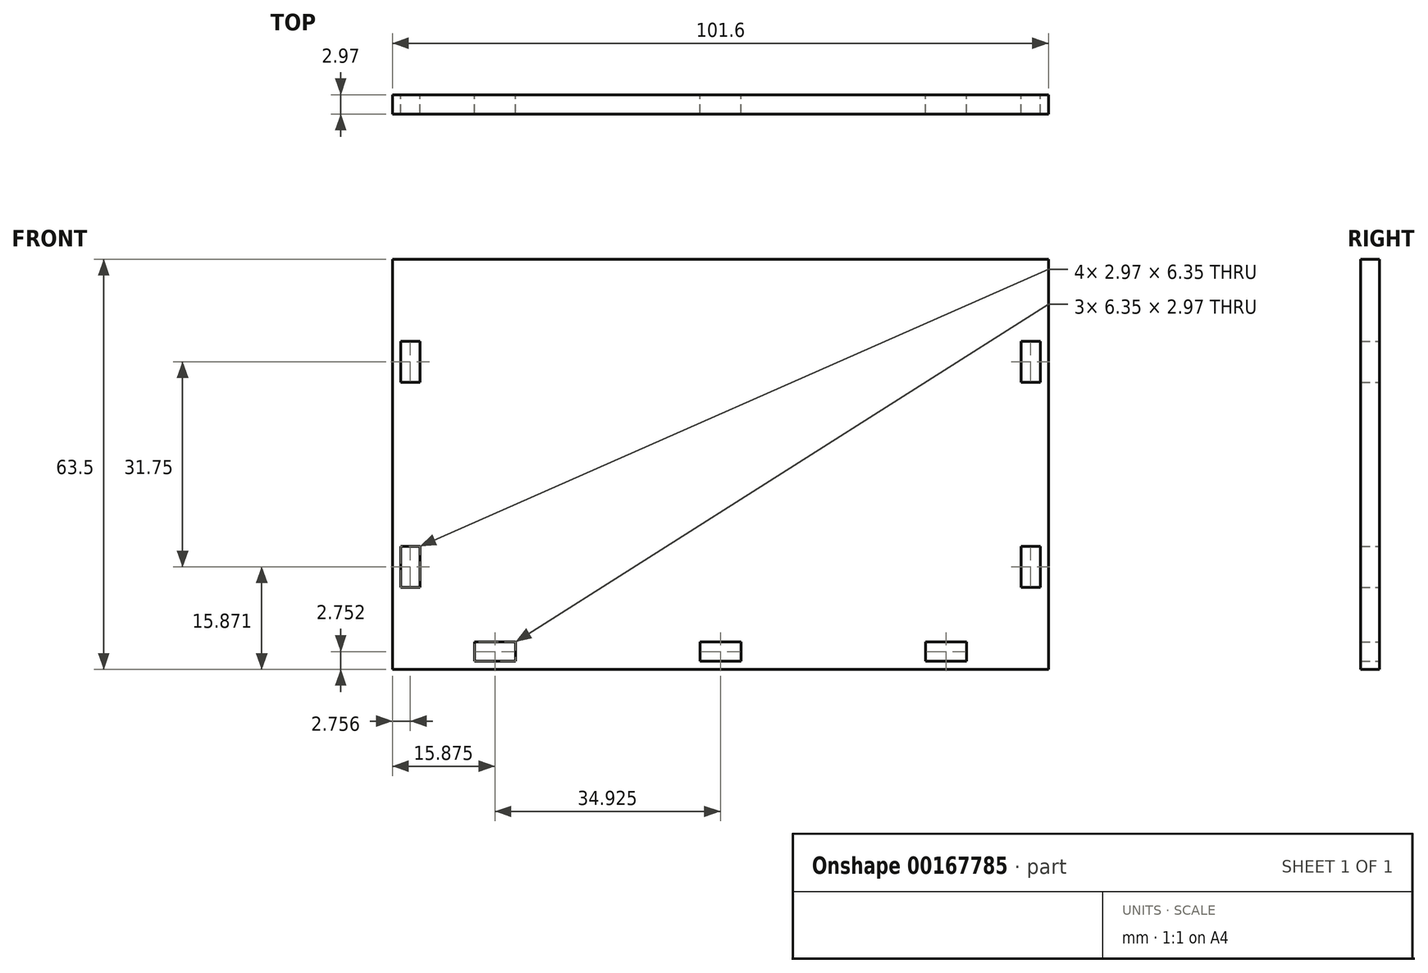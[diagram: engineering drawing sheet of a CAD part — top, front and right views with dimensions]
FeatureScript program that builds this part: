
annotation { "Feature Type Name" : "Feature", "Feature Type Description" : "" }
export const myFeature = defineFeature(function(context is Context, id is Id, definition is map)
    precondition{}
    {
        {
            var Q0;
            Q0=qCreatedBy(makeId("Front.planeOp"),FACE);
            var sketch = newSketch(context, id + "F0", { "sketchPlane" : qUnion([Q0])});
            skLineSegment(sketch, "E0.bottom", {"start": v(50.82, 36.32) * mm, "end": v(-50.78, 36.32) * mm});
            skLineSegment(sketch, "E0.top", {"start": v(50.82, -27.18) * mm, "end": v(-50.78, -27.18) * mm});
            skLineSegment(sketch, "E0.left", {"start": v(50.82, 36.32) * mm, "end": v(50.82, -27.18) * mm});
            skLineSegment(sketch, "E0.right", {"start": v(-50.78, 36.32) * mm, "end": v(-50.78, -27.18) * mm});
            skPoint(sketch, "E0.middle", {"position": v(0.02, 4.57) * mm});
            skLineSegment(sketch, "E1.bottom", {"start": v(-38.08, -22.94) * mm, "end": v(-31.73, -22.94) * mm});
            skLineSegment(sketch, "E1.top", {"start": v(-38.08, -25.91) * mm, "end": v(-31.73, -25.91) * mm});
            skLineSegment(sketch, "E1.left", {"start": v(-38.08, -22.94) * mm, "end": v(-38.08, -25.91) * mm});
            skLineSegment(sketch, "E1.right", {"start": v(-31.73, -22.94) * mm, "end": v(-31.73, -25.91) * mm});
            skLineSegment(sketch, "E2", {"start": v(0.02, 36.32) * mm, "end": v(0.02, -27.18) * mm, "construction": true});
            skLineSegment(sketch, "E3", {"start": v(-50.78, 4.57) * mm, "end": v(50.82, 4.57) * mm, "construction": true});
            skLineSegment(sketch, "E4.MirrorCS", {"start": v(38.12, -22.94) * mm, "end": v(31.77, -22.94) * mm});
            skLineSegment(sketch, "E5.MirrorCS", {"start": v(38.12, -25.91) * mm, "end": v(31.77, -25.91) * mm});
            skLineSegment(sketch, "E6.MirrorCS", {"start": v(31.77, -22.94) * mm, "end": v(31.77, -25.91) * mm});
            skLineSegment(sketch, "E7.MirrorCS", {"start": v(38.12, -22.94) * mm, "end": v(38.12, -25.91) * mm});
            skLineSegment(sketch, "E8.bottom", {"start": v(-3.15, -22.94) * mm, "end": v(3.2, -22.94) * mm});
            skLineSegment(sketch, "E8.top", {"start": v(-3.15, -25.91) * mm, "end": v(3.2, -25.91) * mm});
            skLineSegment(sketch, "E8.left", {"start": v(-3.15, -22.94) * mm, "end": v(-3.15, -25.91) * mm});
            skLineSegment(sketch, "E8.right", {"start": v(3.2, -22.94) * mm, "end": v(3.2, -25.91) * mm});
            skLineSegment(sketch, "E9.bottom", {"start": v(-49.5, 23.62) * mm, "end": v(-46.54, 23.62) * mm});
            skLineSegment(sketch, "E9.top", {"start": v(-49.5, 17.27) * mm, "end": v(-46.54, 17.27) * mm});
            skLineSegment(sketch, "E9.left", {"start": v(-49.5, 23.62) * mm, "end": v(-49.5, 17.27) * mm});
            skLineSegment(sketch, "E9.right", {"start": v(-46.54, 23.62) * mm, "end": v(-46.54, 17.27) * mm});
            skLineSegment(sketch, "E10.MirrorCS", {"start": v(-49.5, -14.48) * mm, "end": v(-49.5, -8.13) * mm});
            skLineSegment(sketch, "E11.MirrorCS", {"start": v(-46.54, -14.48) * mm, "end": v(-46.54, -8.13) * mm});
            skLineSegment(sketch, "E12.MirrorCS", {"start": v(-49.5, -8.13) * mm, "end": v(-46.54, -8.13) * mm});
            skLineSegment(sketch, "E13.MirrorCS", {"start": v(-49.5, -14.48) * mm, "end": v(-46.54, -14.48) * mm});
            skLineSegment(sketch, "E14.MirrorCS", {"start": v(49.55, 23.62) * mm, "end": v(46.58, 23.62) * mm});
            skLineSegment(sketch, "E15.MirrorCS", {"start": v(49.55, 23.62) * mm, "end": v(49.55, 17.27) * mm});
            skLineSegment(sketch, "E16.MirrorCS", {"start": v(46.58, 23.62) * mm, "end": v(46.58, 17.27) * mm});
            skLineSegment(sketch, "E17.MirrorCS", {"start": v(49.55, 17.27) * mm, "end": v(46.58, 17.27) * mm});
            skLineSegment(sketch, "E18.MirrorCS", {"start": v(49.55, -8.13) * mm, "end": v(46.58, -8.13) * mm});
            skLineSegment(sketch, "E19.MirrorCS", {"start": v(49.55, -14.48) * mm, "end": v(49.55, -8.13) * mm});
            skLineSegment(sketch, "E20.MirrorCS", {"start": v(49.55, -14.48) * mm, "end": v(46.58, -14.48) * mm});
            skLineSegment(sketch, "E21.MirrorCS", {"start": v(46.58, -14.48) * mm, "end": v(46.58, -8.13) * mm});
            skLineSegment(sketch, "E22.bottom", {"start": v(-50.78, 36.32) * mm, "end": v(50.82, 36.32) * mm});
            skLineSegment(sketch, "E22.top", {"start": v(-50.78, 155.95) * mm, "end": v(50.82, 155.95) * mm});
            skLineSegment(sketch, "E22.left", {"start": v(-50.78, 36.32) * mm, "end": v(-50.78, 37.08) * mm});
            skLineSegment(sketch, "E22.right", {"start": v(50.82, 36.32) * mm, "end": v(50.82, 37.08) * mm});
            skLineSegment(sketch, "E23", {"start": v(0.02, 36.32) * mm, "end": v(0.02, 155.95) * mm, "construction": true});
            skLineSegment(sketch, "E24.bottom", {"start": v(-3.15, 155.95) * mm, "end": v(3.2, 155.95) * mm});
            skLineSegment(sketch, "E24.top", {"start": v(-3.15, 158.92) * mm, "end": v(3.2, 158.92) * mm});
            skLineSegment(sketch, "E24.left", {"start": v(-3.15, 155.95) * mm, "end": v(-3.15, 158.92) * mm});
            skLineSegment(sketch, "E24.right", {"start": v(3.2, 155.95) * mm, "end": v(3.2, 158.92) * mm});
            skLineSegment(sketch, "E25", {"start": v(-50.78, 153.92) * mm, "end": v(-25.38, 153.92) * mm});
            skLineSegment(sketch, "E26", {"start": v(-50.78, 151.38) * mm, "end": v(-25.38, 151.38) * mm});
            skArc(sketch, "E27", {"start": v(-25.38, 153.92) * mm, "mid": v(-24.1, 152.65) * mm, "end": v(-25.38, 151.38) * mm});
            skLineSegment(sketch, "E28", {"start": v(50.82, 153.68) * mm, "end": v(25.42, 153.92) * mm});
            skLineSegment(sketch, "E29", {"start": v(50.82, 151.38) * mm, "end": v(25.42, 151.38) * mm});
            skLineSegment(sketch, "E30", {"start": v(-21.57, 153.92) * mm, "end": v(21.61, 153.92) * mm});
            skLineSegment(sketch, "E31", {"start": v(-21.57, 151.38) * mm, "end": v(21.61, 151.38) * mm});
            skArc(sketch, "E32", {"start": v(25.42, 153.92) * mm, "mid": v(24.14, 152.65) * mm, "end": v(25.42, 151.38) * mm});
            skPoint(sketch, "E33", {"position": v(0.02, 153.92) * mm});
            skPoint(sketch, "E34", {"position": v(0.02, 151.38) * mm});
            skArc(sketch, "E35", {"start": v(-21.57, 153.92) * mm, "mid": v(-22.84, 152.65) * mm, "end": v(-21.57, 151.38) * mm});
            skArc(sketch, "E36", {"start": v(21.61, 153.92) * mm, "mid": v(22.88, 152.65) * mm, "end": v(21.61, 151.38) * mm});
            skLineSegment(sketch, "E37", {"start": v(-23.47, 155.95) * mm, "end": v(-23.47, 142.74) * mm, "construction": true});
            skLineSegment(sketch, "E38", {"start": v(-45.06, 149.35) * mm, "end": v(-1.88, 149.35) * mm});
            skPoint(sketch, "E38.startSnap0", {"position": v(-23.47, 149.35) * mm});
            skLineSegment(sketch, "E39.0", {"start": v(-45.06, 146.8) * mm, "end": v(-1.88, 146.8) * mm});
            skArc(sketch, "E40", {"start": v(-45.06, 149.35) * mm, "mid": v(-46.33, 148.08) * mm, "end": v(-45.06, 146.8) * mm});
            skArc(sketch, "E41", {"start": v(-1.88, 149.35) * mm, "mid": v(-0.61, 148.08) * mm, "end": v(-1.88, 146.8) * mm});
            skLineSegment(sketch, "E42", {"start": v(-48.5, 149.35) * mm, "end": v(-50.78, 149.35) * mm});
            skLineSegment(sketch, "E43", {"start": v(-48.5, 146.8) * mm, "end": v(-50.78, 146.8) * mm});
            skArc(sketch, "E44", {"start": v(-48.5, 149.35) * mm, "mid": v(-47.22, 148.08) * mm, "end": v(-48.5, 146.8) * mm});
            skArc(sketch, "E45.MirrorCS", {"start": v(1.93, 149.35) * mm, "mid": v(0.66, 148.08) * mm, "end": v(1.93, 146.8) * mm});
            skLineSegment(sketch, "E46.MirrorCS", {"start": v(45.1, 149.35) * mm, "end": v(1.93, 149.35) * mm});
            skLineSegment(sketch, "E47.MirrorCS", {"start": v(45.1, 146.8) * mm, "end": v(1.93, 146.8) * mm});
            skArc(sketch, "E48.MirrorCS", {"start": v(45.1, 149.35) * mm, "mid": v(46.38, 148.08) * mm, "end": v(45.1, 146.8) * mm});
            skLineSegment(sketch, "E49.MirrorCS", {"start": v(48.53, 149.35) * mm, "end": v(50.82, 149.35) * mm});
            skLineSegment(sketch, "E50.MirrorCS", {"start": v(48.53, 146.8) * mm, "end": v(50.82, 146.8) * mm});
            skArc(sketch, "E51", {"start": v(48.53, 149.35) * mm, "mid": v(47.26, 148.08) * mm, "end": v(48.53, 146.8) * mm});
            skLineSegment(sketch, "E52.1.0.0", {"start": v(50.82, 144.54) * mm, "end": v(25.42, 144.77) * mm});
            skLineSegment(sketch, "E52.1.0.1", {"start": v(-21.57, 144.77) * mm, "end": v(21.61, 144.77) * mm});
            skArc(sketch, "E52.1.0.2", {"start": v(25.42, 144.77) * mm, "mid": v(24.14, 143.5) * mm, "end": v(25.42, 142.23) * mm});
            skArc(sketch, "E52.1.0.3", {"start": v(21.61, 144.77) * mm, "mid": v(22.88, 143.5) * mm, "end": v(21.61, 142.23) * mm});
            skLineSegment(sketch, "E52.1.0.4", {"start": v(50.82, 142.23) * mm, "end": v(25.42, 142.23) * mm});
            skLineSegment(sketch, "E52.1.0.5", {"start": v(48.53, 140.2) * mm, "end": v(50.82, 140.2) * mm});
            skArc(sketch, "E52.1.0.6", {"start": v(48.53, 140.2) * mm, "mid": v(47.26, 138.93) * mm, "end": v(48.53, 137.66) * mm});
            skArc(sketch, "E52.1.0.7", {"start": v(45.1, 140.2) * mm, "mid": v(46.38, 138.93) * mm, "end": v(45.1, 137.66) * mm});
            skLineSegment(sketch, "E52.1.0.8", {"start": v(48.53, 137.66) * mm, "end": v(50.82, 137.66) * mm});
            skLineSegment(sketch, "E52.1.0.9", {"start": v(45.1, 137.66) * mm, "end": v(1.93, 137.66) * mm});
            skLineSegment(sketch, "E52.1.0.10", {"start": v(45.1, 140.2) * mm, "end": v(1.93, 140.2) * mm});
            skLineSegment(sketch, "E52.1.0.11", {"start": v(-21.57, 142.23) * mm, "end": v(21.61, 142.23) * mm});
            skArc(sketch, "E52.1.0.12", {"start": v(1.93, 140.2) * mm, "mid": v(0.66, 138.93) * mm, "end": v(1.93, 137.66) * mm});
            skArc(sketch, "E52.1.0.13", {"start": v(-1.88, 140.2) * mm, "mid": v(-0.61, 138.93) * mm, "end": v(-1.88, 137.66) * mm});
            skLineSegment(sketch, "E52.1.0.14", {"start": v(-45.06, 140.2) * mm, "end": v(-1.88, 140.2) * mm});
            skLineSegment(sketch, "E52.1.0.15", {"start": v(-45.06, 137.66) * mm, "end": v(-1.88, 137.66) * mm});
            skLineSegment(sketch, "E52.1.0.16", {"start": v(-50.78, 144.77) * mm, "end": v(-25.38, 144.77) * mm});
            skArc(sketch, "E52.1.0.17", {"start": v(-25.38, 144.77) * mm, "mid": v(-24.1, 143.5) * mm, "end": v(-25.38, 142.23) * mm});
            skArc(sketch, "E52.1.0.18", {"start": v(-21.57, 144.77) * mm, "mid": v(-22.84, 143.5) * mm, "end": v(-21.57, 142.23) * mm});
            skLineSegment(sketch, "E52.1.0.19", {"start": v(-50.78, 142.23) * mm, "end": v(-25.38, 142.23) * mm});
            skArc(sketch, "E52.1.0.20", {"start": v(-45.06, 140.2) * mm, "mid": v(-46.33, 138.93) * mm, "end": v(-45.06, 137.66) * mm});
            skArc(sketch, "E52.1.0.21", {"start": v(-48.5, 140.2) * mm, "mid": v(-47.22, 138.93) * mm, "end": v(-48.5, 137.66) * mm});
            skLineSegment(sketch, "E52.1.0.22", {"start": v(-48.5, 137.66) * mm, "end": v(-50.78, 137.66) * mm});
            skLineSegment(sketch, "E52.1.0.23", {"start": v(-48.5, 140.2) * mm, "end": v(-50.78, 140.2) * mm});
            skLineSegment(sketch, "E52.2.0.0", {"start": v(50.82, 135.4) * mm, "end": v(25.42, 135.63) * mm});
            skLineSegment(sketch, "E52.2.0.1", {"start": v(-21.57, 135.63) * mm, "end": v(21.61, 135.63) * mm});
            skArc(sketch, "E52.2.0.2", {"start": v(25.42, 135.63) * mm, "mid": v(24.14, 134.36) * mm, "end": v(25.42, 133.1) * mm});
            skArc(sketch, "E52.2.0.3", {"start": v(21.61, 135.63) * mm, "mid": v(22.88, 134.36) * mm, "end": v(21.61, 133.09) * mm});
            skLineSegment(sketch, "E52.2.0.4", {"start": v(50.82, 133.09) * mm, "end": v(25.42, 133.1) * mm});
            skLineSegment(sketch, "E52.2.0.5", {"start": v(48.53, 131.06) * mm, "end": v(50.82, 131.06) * mm});
            skArc(sketch, "E52.2.0.6", {"start": v(48.53, 131.06) * mm, "mid": v(47.26, 129.79) * mm, "end": v(48.53, 128.52) * mm});
            skArc(sketch, "E52.2.0.7", {"start": v(45.1, 131.06) * mm, "mid": v(46.38, 129.79) * mm, "end": v(45.1, 128.52) * mm});
            skLineSegment(sketch, "E52.2.0.8", {"start": v(48.53, 128.52) * mm, "end": v(50.82, 128.52) * mm});
            skLineSegment(sketch, "E52.2.0.9", {"start": v(45.1, 128.52) * mm, "end": v(1.93, 128.52) * mm});
            skLineSegment(sketch, "E52.2.0.10", {"start": v(45.1, 131.06) * mm, "end": v(1.93, 131.06) * mm});
            skLineSegment(sketch, "E52.2.0.11", {"start": v(-21.57, 133.09) * mm, "end": v(21.61, 133.09) * mm});
            skArc(sketch, "E52.2.0.12", {"start": v(1.93, 131.06) * mm, "mid": v(0.66, 129.79) * mm, "end": v(1.93, 128.52) * mm});
            skArc(sketch, "E52.2.0.13", {"start": v(-1.88, 131.06) * mm, "mid": v(-0.61, 129.79) * mm, "end": v(-1.88, 128.52) * mm});
            skLineSegment(sketch, "E52.2.0.14", {"start": v(-45.06, 131.06) * mm, "end": v(-1.88, 131.06) * mm});
            skLineSegment(sketch, "E52.2.0.15", {"start": v(-45.06, 128.52) * mm, "end": v(-1.88, 128.52) * mm});
            skLineSegment(sketch, "E52.2.0.16", {"start": v(-50.78, 135.63) * mm, "end": v(-25.38, 135.63) * mm});
            skArc(sketch, "E52.2.0.17", {"start": v(-25.38, 135.63) * mm, "mid": v(-24.1, 134.36) * mm, "end": v(-25.38, 133.09) * mm});
            skArc(sketch, "E52.2.0.18", {"start": v(-21.57, 135.63) * mm, "mid": v(-22.84, 134.36) * mm, "end": v(-21.57, 133.09) * mm});
            skLineSegment(sketch, "E52.2.0.19", {"start": v(-50.78, 133.09) * mm, "end": v(-25.38, 133.09) * mm});
            skArc(sketch, "E52.2.0.20", {"start": v(-45.06, 131.06) * mm, "mid": v(-46.33, 129.79) * mm, "end": v(-45.06, 128.52) * mm});
            skArc(sketch, "E52.2.0.21", {"start": v(-48.5, 131.06) * mm, "mid": v(-47.22, 129.79) * mm, "end": v(-48.5, 128.52) * mm});
            skLineSegment(sketch, "E52.2.0.22", {"start": v(-48.5, 128.52) * mm, "end": v(-50.78, 128.52) * mm});
            skLineSegment(sketch, "E52.2.0.23", {"start": v(-48.5, 131.06) * mm, "end": v(-50.78, 131.06) * mm});
            skLineSegment(sketch, "E52.3.0.0", {"start": v(50.82, 126.25) * mm, "end": v(25.42, 126.49) * mm});
            skLineSegment(sketch, "E52.3.0.1", {"start": v(-21.57, 126.49) * mm, "end": v(21.61, 126.49) * mm});
            skArc(sketch, "E52.3.0.2", {"start": v(25.42, 126.49) * mm, "mid": v(24.14, 125.22) * mm, "end": v(25.42, 123.95) * mm});
            skArc(sketch, "E52.3.0.3", {"start": v(21.61, 126.49) * mm, "mid": v(22.88, 125.22) * mm, "end": v(21.61, 123.95) * mm});
            skLineSegment(sketch, "E52.3.0.4", {"start": v(50.82, 123.95) * mm, "end": v(25.42, 123.95) * mm});
            skLineSegment(sketch, "E52.3.0.5", {"start": v(48.53, 121.91) * mm, "end": v(50.82, 121.91) * mm});
            skArc(sketch, "E52.3.0.6", {"start": v(48.53, 121.91) * mm, "mid": v(47.26, 120.64) * mm, "end": v(48.53, 119.37) * mm});
            skArc(sketch, "E52.3.0.7", {"start": v(45.1, 121.91) * mm, "mid": v(46.38, 120.64) * mm, "end": v(45.1, 119.37) * mm});
            skLineSegment(sketch, "E52.3.0.8", {"start": v(48.53, 119.37) * mm, "end": v(50.82, 119.37) * mm});
            skLineSegment(sketch, "E52.3.0.9", {"start": v(45.1, 119.37) * mm, "end": v(1.93, 119.37) * mm});
            skLineSegment(sketch, "E52.3.0.10", {"start": v(45.1, 121.91) * mm, "end": v(1.93, 121.91) * mm});
            skLineSegment(sketch, "E52.3.0.11", {"start": v(-21.57, 123.95) * mm, "end": v(21.61, 123.95) * mm});
            skArc(sketch, "E52.3.0.12", {"start": v(1.93, 121.91) * mm, "mid": v(0.66, 120.64) * mm, "end": v(1.93, 119.37) * mm});
            skArc(sketch, "E52.3.0.13", {"start": v(-1.88, 121.91) * mm, "mid": v(-0.61, 120.64) * mm, "end": v(-1.88, 119.37) * mm});
            skLineSegment(sketch, "E52.3.0.14", {"start": v(-45.06, 121.91) * mm, "end": v(-1.88, 121.91) * mm});
            skLineSegment(sketch, "E52.3.0.15", {"start": v(-45.06, 119.37) * mm, "end": v(-1.88, 119.37) * mm});
            skLineSegment(sketch, "E52.3.0.16", {"start": v(-50.78, 126.49) * mm, "end": v(-25.38, 126.49) * mm});
            skArc(sketch, "E52.3.0.17", {"start": v(-25.38, 126.49) * mm, "mid": v(-24.1, 125.22) * mm, "end": v(-25.38, 123.95) * mm});
            skArc(sketch, "E52.3.0.18", {"start": v(-21.57, 126.49) * mm, "mid": v(-22.84, 125.22) * mm, "end": v(-21.57, 123.95) * mm});
            skLineSegment(sketch, "E52.3.0.19", {"start": v(-50.78, 123.95) * mm, "end": v(-25.38, 123.95) * mm});
            skArc(sketch, "E52.3.0.20", {"start": v(-45.06, 121.91) * mm, "mid": v(-46.33, 120.64) * mm, "end": v(-45.06, 119.37) * mm});
            skArc(sketch, "E52.3.0.21", {"start": v(-48.5, 121.91) * mm, "mid": v(-47.22, 120.64) * mm, "end": v(-48.5, 119.37) * mm});
            skLineSegment(sketch, "E52.3.0.22", {"start": v(-48.5, 119.37) * mm, "end": v(-50.78, 119.37) * mm});
            skLineSegment(sketch, "E52.3.0.23", {"start": v(-48.5, 121.91) * mm, "end": v(-50.78, 121.91) * mm});
            skLineSegment(sketch, "E52.4.0.0", {"start": v(50.82, 117.1) * mm, "end": v(25.42, 117.34) * mm});
            skLineSegment(sketch, "E52.4.0.1", {"start": v(-21.57, 117.34) * mm, "end": v(21.61, 117.34) * mm});
            skArc(sketch, "E52.4.0.2", {"start": v(25.42, 117.34) * mm, "mid": v(24.14, 116.07) * mm, "end": v(25.42, 114.8) * mm});
            skArc(sketch, "E52.4.0.3", {"start": v(21.61, 117.34) * mm, "mid": v(22.88, 116.07) * mm, "end": v(21.61, 114.8) * mm});
            skLineSegment(sketch, "E52.4.0.4", {"start": v(50.82, 114.8) * mm, "end": v(25.42, 114.8) * mm});
            skLineSegment(sketch, "E52.4.0.5", {"start": v(48.53, 112.77) * mm, "end": v(50.82, 112.77) * mm});
            skArc(sketch, "E52.4.0.6", {"start": v(48.53, 112.77) * mm, "mid": v(47.26, 111.5) * mm, "end": v(48.53, 110.23) * mm});
            skArc(sketch, "E52.4.0.7", {"start": v(45.1, 112.77) * mm, "mid": v(46.38, 111.5) * mm, "end": v(45.1, 110.23) * mm});
            skLineSegment(sketch, "E52.4.0.8", {"start": v(48.53, 110.23) * mm, "end": v(50.82, 110.23) * mm});
            skLineSegment(sketch, "E52.4.0.9", {"start": v(45.1, 110.23) * mm, "end": v(1.93, 110.23) * mm});
            skLineSegment(sketch, "E52.4.0.10", {"start": v(45.1, 112.77) * mm, "end": v(1.93, 112.77) * mm});
            skLineSegment(sketch, "E52.4.0.11", {"start": v(-21.57, 114.8) * mm, "end": v(21.61, 114.8) * mm});
            skArc(sketch, "E52.4.0.12", {"start": v(1.93, 112.77) * mm, "mid": v(0.66, 111.5) * mm, "end": v(1.93, 110.23) * mm});
            skArc(sketch, "E52.4.0.13", {"start": v(-1.88, 112.77) * mm, "mid": v(-0.61, 111.5) * mm, "end": v(-1.88, 110.23) * mm});
            skLineSegment(sketch, "E52.4.0.14", {"start": v(-45.06, 112.77) * mm, "end": v(-1.88, 112.77) * mm});
            skLineSegment(sketch, "E52.4.0.15", {"start": v(-45.06, 110.23) * mm, "end": v(-1.88, 110.23) * mm});
            skLineSegment(sketch, "E52.4.0.16", {"start": v(-50.78, 117.34) * mm, "end": v(-25.38, 117.34) * mm});
            skArc(sketch, "E52.4.0.17", {"start": v(-25.38, 117.34) * mm, "mid": v(-24.1, 116.07) * mm, "end": v(-25.38, 114.8) * mm});
            skArc(sketch, "E52.4.0.18", {"start": v(-21.57, 117.34) * mm, "mid": v(-22.84, 116.07) * mm, "end": v(-21.57, 114.8) * mm});
            skLineSegment(sketch, "E52.4.0.19", {"start": v(-50.78, 114.8) * mm, "end": v(-25.38, 114.8) * mm});
            skArc(sketch, "E52.4.0.20", {"start": v(-45.06, 112.77) * mm, "mid": v(-46.33, 111.5) * mm, "end": v(-45.06, 110.23) * mm});
            skArc(sketch, "E52.4.0.21", {"start": v(-48.5, 112.77) * mm, "mid": v(-47.22, 111.5) * mm, "end": v(-48.5, 110.23) * mm});
            skLineSegment(sketch, "E52.4.0.22", {"start": v(-48.5, 110.23) * mm, "end": v(-50.78, 110.23) * mm});
            skLineSegment(sketch, "E52.4.0.23", {"start": v(-48.5, 112.77) * mm, "end": v(-50.78, 112.77) * mm});
            skLineSegment(sketch, "E52.5.0.0", {"start": v(50.82, 107.96) * mm, "end": v(25.42, 108.2) * mm});
            skLineSegment(sketch, "E52.5.0.1", {"start": v(-21.57, 108.2) * mm, "end": v(21.61, 108.2) * mm});
            skArc(sketch, "E52.5.0.2", {"start": v(25.42, 108.2) * mm, "mid": v(24.14, 106.93) * mm, "end": v(25.42, 105.66) * mm});
            skArc(sketch, "E52.5.0.3", {"start": v(21.61, 108.2) * mm, "mid": v(22.88, 106.93) * mm, "end": v(21.61, 105.66) * mm});
            skLineSegment(sketch, "E52.5.0.4", {"start": v(50.82, 105.66) * mm, "end": v(25.42, 105.66) * mm});
            skLineSegment(sketch, "E52.5.0.5", {"start": v(48.53, 103.63) * mm, "end": v(50.82, 103.63) * mm});
            skArc(sketch, "E52.5.0.6", {"start": v(48.53, 103.63) * mm, "mid": v(47.26, 102.36) * mm, "end": v(48.53, 101.09) * mm});
            skArc(sketch, "E52.5.0.7", {"start": v(45.1, 103.63) * mm, "mid": v(46.38, 102.36) * mm, "end": v(45.1, 101.09) * mm});
            skLineSegment(sketch, "E52.5.0.8", {"start": v(48.53, 101.09) * mm, "end": v(50.82, 101.09) * mm});
            skLineSegment(sketch, "E52.5.0.9", {"start": v(45.1, 101.09) * mm, "end": v(1.93, 101.09) * mm});
            skLineSegment(sketch, "E52.5.0.10", {"start": v(45.1, 103.63) * mm, "end": v(1.93, 103.63) * mm});
            skLineSegment(sketch, "E52.5.0.11", {"start": v(-21.57, 105.66) * mm, "end": v(21.61, 105.66) * mm});
            skArc(sketch, "E52.5.0.12", {"start": v(1.93, 103.63) * mm, "mid": v(0.66, 102.36) * mm, "end": v(1.93, 101.09) * mm});
            skArc(sketch, "E52.5.0.13", {"start": v(-1.88, 103.63) * mm, "mid": v(-0.61, 102.36) * mm, "end": v(-1.88, 101.09) * mm});
            skLineSegment(sketch, "E52.5.0.14", {"start": v(-45.06, 103.63) * mm, "end": v(-1.88, 103.63) * mm});
            skLineSegment(sketch, "E52.5.0.15", {"start": v(-45.06, 101.09) * mm, "end": v(-1.88, 101.09) * mm});
            skLineSegment(sketch, "E52.5.0.16", {"start": v(-50.78, 108.2) * mm, "end": v(-25.38, 108.2) * mm});
            skArc(sketch, "E52.5.0.17", {"start": v(-25.38, 108.2) * mm, "mid": v(-24.1, 106.93) * mm, "end": v(-25.38, 105.66) * mm});
            skArc(sketch, "E52.5.0.18", {"start": v(-21.57, 108.2) * mm, "mid": v(-22.84, 106.93) * mm, "end": v(-21.57, 105.66) * mm});
            skLineSegment(sketch, "E52.5.0.19", {"start": v(-50.78, 105.66) * mm, "end": v(-25.38, 105.66) * mm});
            skArc(sketch, "E52.5.0.20", {"start": v(-45.06, 103.63) * mm, "mid": v(-46.33, 102.36) * mm, "end": v(-45.06, 101.09) * mm});
            skArc(sketch, "E52.5.0.21", {"start": v(-48.5, 103.63) * mm, "mid": v(-47.22, 102.36) * mm, "end": v(-48.5, 101.09) * mm});
            skLineSegment(sketch, "E52.5.0.22", {"start": v(-48.5, 101.09) * mm, "end": v(-50.78, 101.09) * mm});
            skLineSegment(sketch, "E52.5.0.23", {"start": v(-48.5, 103.63) * mm, "end": v(-50.78, 103.63) * mm});
            skLineSegment(sketch, "E52.6.0.0", {"start": v(50.82, 98.82) * mm, "end": v(25.42, 99.05) * mm});
            skLineSegment(sketch, "E52.6.0.1", {"start": v(-21.57, 99.05) * mm, "end": v(21.61, 99.05) * mm});
            skArc(sketch, "E52.6.0.2", {"start": v(25.42, 99.05) * mm, "mid": v(24.14, 97.78) * mm, "end": v(25.42, 96.51) * mm});
            skArc(sketch, "E52.6.0.3", {"start": v(21.61, 99.05) * mm, "mid": v(22.88, 97.78) * mm, "end": v(21.61, 96.51) * mm});
            skLineSegment(sketch, "E52.6.0.4", {"start": v(50.82, 96.51) * mm, "end": v(25.42, 96.51) * mm});
            skLineSegment(sketch, "E52.6.0.5", {"start": v(48.53, 94.48) * mm, "end": v(50.82, 94.48) * mm});
            skArc(sketch, "E52.6.0.6", {"start": v(48.53, 94.48) * mm, "mid": v(47.26, 93.21) * mm, "end": v(48.53, 91.94) * mm});
            skArc(sketch, "E52.6.0.7", {"start": v(45.1, 94.48) * mm, "mid": v(46.38, 93.21) * mm, "end": v(45.1, 91.94) * mm});
            skLineSegment(sketch, "E52.6.0.8", {"start": v(48.53, 91.94) * mm, "end": v(50.82, 91.94) * mm});
            skLineSegment(sketch, "E52.6.0.9", {"start": v(45.1, 91.94) * mm, "end": v(1.93, 91.94) * mm});
            skLineSegment(sketch, "E52.6.0.10", {"start": v(45.1, 94.48) * mm, "end": v(1.93, 94.48) * mm});
            skLineSegment(sketch, "E52.6.0.11", {"start": v(-21.57, 96.51) * mm, "end": v(21.61, 96.51) * mm});
            skArc(sketch, "E52.6.0.12", {"start": v(1.93, 94.48) * mm, "mid": v(0.66, 93.21) * mm, "end": v(1.93, 91.94) * mm});
            skArc(sketch, "E52.6.0.13", {"start": v(-1.88, 94.48) * mm, "mid": v(-0.61, 93.21) * mm, "end": v(-1.88, 91.94) * mm});
            skLineSegment(sketch, "E52.6.0.14", {"start": v(-45.06, 94.48) * mm, "end": v(-1.88, 94.48) * mm});
            skLineSegment(sketch, "E52.6.0.15", {"start": v(-45.06, 91.94) * mm, "end": v(-1.88, 91.94) * mm});
            skLineSegment(sketch, "E52.6.0.16", {"start": v(-50.78, 99.05) * mm, "end": v(-25.38, 99.05) * mm});
            skArc(sketch, "E52.6.0.17", {"start": v(-25.38, 99.05) * mm, "mid": v(-24.1, 97.78) * mm, "end": v(-25.38, 96.51) * mm});
            skArc(sketch, "E52.6.0.18", {"start": v(-21.57, 99.05) * mm, "mid": v(-22.84, 97.78) * mm, "end": v(-21.57, 96.51) * mm});
            skLineSegment(sketch, "E52.6.0.19", {"start": v(-50.78, 96.51) * mm, "end": v(-25.38, 96.51) * mm});
            skArc(sketch, "E52.6.0.20", {"start": v(-45.06, 94.48) * mm, "mid": v(-46.33, 93.21) * mm, "end": v(-45.06, 91.94) * mm});
            skArc(sketch, "E52.6.0.21", {"start": v(-48.5, 94.48) * mm, "mid": v(-47.22, 93.21) * mm, "end": v(-48.5, 91.94) * mm});
            skLineSegment(sketch, "E52.6.0.22", {"start": v(-48.5, 91.94) * mm, "end": v(-50.78, 91.94) * mm});
            skLineSegment(sketch, "E52.6.0.23", {"start": v(-48.5, 94.48) * mm, "end": v(-50.78, 94.48) * mm});
            skLineSegment(sketch, "E52.7.0.0", {"start": v(50.82, 89.68) * mm, "end": v(25.42, 89.91) * mm});
            skLineSegment(sketch, "E52.7.0.1", {"start": v(-21.57, 89.9) * mm, "end": v(21.61, 89.9) * mm});
            skArc(sketch, "E52.7.0.2", {"start": v(25.42, 89.91) * mm, "mid": v(24.14, 88.64) * mm, "end": v(25.42, 87.37) * mm});
            skArc(sketch, "E52.7.0.3", {"start": v(21.61, 89.9) * mm, "mid": v(22.88, 88.64) * mm, "end": v(21.61, 87.37) * mm});
            skLineSegment(sketch, "E52.7.0.4", {"start": v(50.82, 87.37) * mm, "end": v(25.42, 87.37) * mm});
            skLineSegment(sketch, "E52.7.0.5", {"start": v(48.53, 85.34) * mm, "end": v(50.82, 85.34) * mm});
            skArc(sketch, "E52.7.0.6", {"start": v(48.53, 85.34) * mm, "mid": v(47.26, 84.07) * mm, "end": v(48.53, 82.8) * mm});
            skArc(sketch, "E52.7.0.7", {"start": v(45.1, 85.34) * mm, "mid": v(46.38, 84.07) * mm, "end": v(45.1, 82.8) * mm});
            skLineSegment(sketch, "E52.7.0.8", {"start": v(48.53, 82.8) * mm, "end": v(50.82, 82.8) * mm});
            skLineSegment(sketch, "E52.7.0.9", {"start": v(45.1, 82.8) * mm, "end": v(1.93, 82.8) * mm});
            skLineSegment(sketch, "E52.7.0.10", {"start": v(45.1, 85.34) * mm, "end": v(1.93, 85.34) * mm});
            skLineSegment(sketch, "E52.7.0.11", {"start": v(-21.57, 87.37) * mm, "end": v(21.61, 87.37) * mm});
            skArc(sketch, "E52.7.0.12", {"start": v(1.93, 85.34) * mm, "mid": v(0.66, 84.07) * mm, "end": v(1.93, 82.8) * mm});
            skArc(sketch, "E52.7.0.13", {"start": v(-1.88, 85.34) * mm, "mid": v(-0.61, 84.07) * mm, "end": v(-1.88, 82.8) * mm});
            skLineSegment(sketch, "E52.7.0.14", {"start": v(-45.06, 85.34) * mm, "end": v(-1.88, 85.34) * mm});
            skLineSegment(sketch, "E52.7.0.15", {"start": v(-45.06, 82.8) * mm, "end": v(-1.88, 82.8) * mm});
            skLineSegment(sketch, "E52.7.0.16", {"start": v(-50.78, 89.9) * mm, "end": v(-25.38, 89.9) * mm});
            skArc(sketch, "E52.7.0.17", {"start": v(-25.38, 89.9) * mm, "mid": v(-24.1, 88.64) * mm, "end": v(-25.38, 87.37) * mm});
            skArc(sketch, "E52.7.0.18", {"start": v(-21.57, 89.9) * mm, "mid": v(-22.84, 88.64) * mm, "end": v(-21.57, 87.37) * mm});
            skLineSegment(sketch, "E52.7.0.19", {"start": v(-50.78, 87.37) * mm, "end": v(-25.38, 87.37) * mm});
            skArc(sketch, "E52.7.0.20", {"start": v(-45.06, 85.34) * mm, "mid": v(-46.33, 84.07) * mm, "end": v(-45.06, 82.8) * mm});
            skArc(sketch, "E52.7.0.21", {"start": v(-48.5, 85.34) * mm, "mid": v(-47.22, 84.07) * mm, "end": v(-48.5, 82.8) * mm});
            skLineSegment(sketch, "E52.7.0.22", {"start": v(-48.5, 82.8) * mm, "end": v(-50.78, 82.8) * mm});
            skLineSegment(sketch, "E52.7.0.23", {"start": v(-48.5, 85.34) * mm, "end": v(-50.78, 85.34) * mm});
            skLineSegment(sketch, "E52.8.0.0", {"start": v(50.82, 80.53) * mm, "end": v(25.42, 80.77) * mm});
            skLineSegment(sketch, "E52.8.0.1", {"start": v(-21.57, 80.77) * mm, "end": v(21.61, 80.77) * mm});
            skArc(sketch, "E52.8.0.2", {"start": v(25.42, 80.77) * mm, "mid": v(24.14, 79.5) * mm, "end": v(25.42, 78.23) * mm});
            skArc(sketch, "E52.8.0.3", {"start": v(21.61, 80.77) * mm, "mid": v(22.88, 79.5) * mm, "end": v(21.61, 78.23) * mm});
            skLineSegment(sketch, "E52.8.0.4", {"start": v(50.82, 78.23) * mm, "end": v(25.42, 78.23) * mm});
            skLineSegment(sketch, "E52.8.0.5", {"start": v(48.53, 76.2) * mm, "end": v(50.82, 76.2) * mm});
            skArc(sketch, "E52.8.0.6", {"start": v(48.53, 76.2) * mm, "mid": v(47.26, 74.92) * mm, "end": v(48.53, 73.65) * mm});
            skArc(sketch, "E52.8.0.7", {"start": v(45.1, 76.2) * mm, "mid": v(46.38, 74.92) * mm, "end": v(45.1, 73.65) * mm});
            skLineSegment(sketch, "E52.8.0.8", {"start": v(48.53, 73.65) * mm, "end": v(50.82, 73.65) * mm});
            skLineSegment(sketch, "E52.8.0.9", {"start": v(45.1, 73.65) * mm, "end": v(1.93, 73.65) * mm});
            skLineSegment(sketch, "E52.8.0.10", {"start": v(45.1, 76.2) * mm, "end": v(1.93, 76.2) * mm});
            skLineSegment(sketch, "E52.8.0.11", {"start": v(-21.57, 78.23) * mm, "end": v(21.61, 78.23) * mm});
            skArc(sketch, "E52.8.0.12", {"start": v(1.93, 76.2) * mm, "mid": v(0.66, 74.92) * mm, "end": v(1.93, 73.65) * mm});
            skArc(sketch, "E52.8.0.13", {"start": v(-1.88, 76.2) * mm, "mid": v(-0.61, 74.92) * mm, "end": v(-1.88, 73.65) * mm});
            skLineSegment(sketch, "E52.8.0.14", {"start": v(-45.06, 76.2) * mm, "end": v(-1.88, 76.2) * mm});
            skLineSegment(sketch, "E52.8.0.15", {"start": v(-45.06, 73.65) * mm, "end": v(-1.88, 73.65) * mm});
            skLineSegment(sketch, "E52.8.0.16", {"start": v(-50.78, 80.77) * mm, "end": v(-25.38, 80.77) * mm});
            skArc(sketch, "E52.8.0.17", {"start": v(-25.38, 80.77) * mm, "mid": v(-24.1, 79.5) * mm, "end": v(-25.38, 78.23) * mm});
            skArc(sketch, "E52.8.0.18", {"start": v(-21.57, 80.77) * mm, "mid": v(-22.84, 79.5) * mm, "end": v(-21.57, 78.23) * mm});
            skLineSegment(sketch, "E52.8.0.19", {"start": v(-50.78, 78.23) * mm, "end": v(-25.38, 78.23) * mm});
            skArc(sketch, "E52.8.0.20", {"start": v(-45.06, 76.2) * mm, "mid": v(-46.33, 74.92) * mm, "end": v(-45.06, 73.65) * mm});
            skArc(sketch, "E52.8.0.21", {"start": v(-48.5, 76.2) * mm, "mid": v(-47.22, 74.92) * mm, "end": v(-48.5, 73.65) * mm});
            skLineSegment(sketch, "E52.8.0.22", {"start": v(-48.5, 73.65) * mm, "end": v(-50.78, 73.65) * mm});
            skLineSegment(sketch, "E52.8.0.23", {"start": v(-48.5, 76.2) * mm, "end": v(-50.78, 76.2) * mm});
            skLineSegment(sketch, "E52.9.0.0", {"start": v(50.82, 71.39) * mm, "end": v(25.42, 71.62) * mm});
            skLineSegment(sketch, "E52.9.0.1", {"start": v(-21.57, 71.62) * mm, "end": v(21.61, 71.62) * mm});
            skArc(sketch, "E52.9.0.2", {"start": v(25.42, 71.62) * mm, "mid": v(24.14, 70.35) * mm, "end": v(25.42, 69.08) * mm});
            skArc(sketch, "E52.9.0.3", {"start": v(21.61, 71.62) * mm, "mid": v(22.88, 70.35) * mm, "end": v(21.61, 69.08) * mm});
            skLineSegment(sketch, "E52.9.0.4", {"start": v(50.82, 69.08) * mm, "end": v(25.42, 69.08) * mm});
            skLineSegment(sketch, "E52.9.0.5", {"start": v(48.53, 67.05) * mm, "end": v(50.82, 67.05) * mm});
            skArc(sketch, "E52.9.0.6", {"start": v(48.53, 67.05) * mm, "mid": v(47.26, 65.78) * mm, "end": v(48.53, 64.5) * mm});
            skArc(sketch, "E52.9.0.7", {"start": v(45.1, 67.05) * mm, "mid": v(46.38, 65.78) * mm, "end": v(45.1, 64.5) * mm});
            skLineSegment(sketch, "E52.9.0.8", {"start": v(48.53, 64.5) * mm, "end": v(50.82, 64.5) * mm});
            skLineSegment(sketch, "E52.9.0.9", {"start": v(45.1, 64.5) * mm, "end": v(1.93, 64.5) * mm});
            skLineSegment(sketch, "E52.9.0.10", {"start": v(45.1, 67.05) * mm, "end": v(1.93, 67.05) * mm});
            skLineSegment(sketch, "E52.9.0.11", {"start": v(-21.57, 69.08) * mm, "end": v(21.61, 69.08) * mm});
            skArc(sketch, "E52.9.0.12", {"start": v(1.93, 67.05) * mm, "mid": v(0.66, 65.78) * mm, "end": v(1.93, 64.5) * mm});
            skArc(sketch, "E52.9.0.13", {"start": v(-1.88, 67.05) * mm, "mid": v(-0.61, 65.78) * mm, "end": v(-1.88, 64.5) * mm});
            skLineSegment(sketch, "E52.9.0.14", {"start": v(-45.06, 67.05) * mm, "end": v(-1.88, 67.05) * mm});
            skLineSegment(sketch, "E52.9.0.15", {"start": v(-45.06, 64.5) * mm, "end": v(-1.88, 64.5) * mm});
            skLineSegment(sketch, "E52.9.0.16", {"start": v(-50.78, 71.62) * mm, "end": v(-25.38, 71.62) * mm});
            skArc(sketch, "E52.9.0.17", {"start": v(-25.38, 71.62) * mm, "mid": v(-24.1, 70.35) * mm, "end": v(-25.38, 69.08) * mm});
            skArc(sketch, "E52.9.0.18", {"start": v(-21.57, 71.62) * mm, "mid": v(-22.84, 70.35) * mm, "end": v(-21.57, 69.08) * mm});
            skLineSegment(sketch, "E52.9.0.19", {"start": v(-50.78, 69.08) * mm, "end": v(-25.38, 69.08) * mm});
            skArc(sketch, "E52.9.0.20", {"start": v(-45.06, 67.05) * mm, "mid": v(-46.33, 65.78) * mm, "end": v(-45.06, 64.5) * mm});
            skArc(sketch, "E52.9.0.21", {"start": v(-48.5, 67.05) * mm, "mid": v(-47.22, 65.78) * mm, "end": v(-48.5, 64.5) * mm});
            skLineSegment(sketch, "E52.9.0.22", {"start": v(-48.5, 64.5) * mm, "end": v(-50.78, 64.5) * mm});
            skLineSegment(sketch, "E52.9.0.23", {"start": v(-48.5, 67.05) * mm, "end": v(-50.78, 67.05) * mm});
            skLineSegment(sketch, "E52.10.0.0", {"start": v(50.82, 62.24) * mm, "end": v(25.42, 62.48) * mm});
            skLineSegment(sketch, "E52.10.0.1", {"start": v(-21.57, 62.48) * mm, "end": v(21.61, 62.48) * mm});
            skArc(sketch, "E52.10.0.2", {"start": v(25.42, 62.48) * mm, "mid": v(24.14, 61.2) * mm, "end": v(25.42, 59.94) * mm});
            skArc(sketch, "E52.10.0.3", {"start": v(21.61, 62.48) * mm, "mid": v(22.88, 61.2) * mm, "end": v(21.61, 59.94) * mm});
            skLineSegment(sketch, "E52.10.0.4", {"start": v(50.82, 59.94) * mm, "end": v(25.42, 59.94) * mm});
            skLineSegment(sketch, "E52.10.0.5", {"start": v(48.53, 57.9) * mm, "end": v(50.82, 57.9) * mm});
            skArc(sketch, "E52.10.0.6", {"start": v(48.53, 57.9) * mm, "mid": v(47.26, 56.64) * mm, "end": v(48.53, 55.37) * mm});
            skArc(sketch, "E52.10.0.7", {"start": v(45.1, 57.9) * mm, "mid": v(46.38, 56.64) * mm, "end": v(45.1, 55.37) * mm});
            skLineSegment(sketch, "E52.10.0.8", {"start": v(48.53, 55.37) * mm, "end": v(50.82, 55.37) * mm});
            skLineSegment(sketch, "E52.10.0.9", {"start": v(45.1, 55.37) * mm, "end": v(1.93, 55.37) * mm});
            skLineSegment(sketch, "E52.10.0.10", {"start": v(45.1, 57.9) * mm, "end": v(1.93, 57.9) * mm});
            skLineSegment(sketch, "E52.10.0.11", {"start": v(-21.57, 59.94) * mm, "end": v(21.61, 59.94) * mm});
            skArc(sketch, "E52.10.0.12", {"start": v(1.93, 57.9) * mm, "mid": v(0.66, 56.64) * mm, "end": v(1.93, 55.37) * mm});
            skArc(sketch, "E52.10.0.13", {"start": v(-1.88, 57.9) * mm, "mid": v(-0.61, 56.64) * mm, "end": v(-1.88, 55.37) * mm});
            skLineSegment(sketch, "E52.10.0.14", {"start": v(-45.06, 57.9) * mm, "end": v(-1.88, 57.9) * mm});
            skLineSegment(sketch, "E52.10.0.15", {"start": v(-45.06, 55.37) * mm, "end": v(-1.88, 55.37) * mm});
            skLineSegment(sketch, "E52.10.0.16", {"start": v(-50.78, 62.48) * mm, "end": v(-25.38, 62.48) * mm});
            skArc(sketch, "E52.10.0.17", {"start": v(-25.38, 62.48) * mm, "mid": v(-24.1, 61.2) * mm, "end": v(-25.38, 59.94) * mm});
            skArc(sketch, "E52.10.0.18", {"start": v(-21.57, 62.48) * mm, "mid": v(-22.84, 61.2) * mm, "end": v(-21.57, 59.94) * mm});
            skLineSegment(sketch, "E52.10.0.19", {"start": v(-50.78, 59.94) * mm, "end": v(-25.38, 59.94) * mm});
            skArc(sketch, "E52.10.0.20", {"start": v(-45.06, 57.9) * mm, "mid": v(-46.33, 56.64) * mm, "end": v(-45.06, 55.37) * mm});
            skArc(sketch, "E52.10.0.21", {"start": v(-48.5, 57.9) * mm, "mid": v(-47.22, 56.64) * mm, "end": v(-48.5, 55.37) * mm});
            skLineSegment(sketch, "E52.10.0.22", {"start": v(-48.5, 55.37) * mm, "end": v(-50.78, 55.37) * mm});
            skLineSegment(sketch, "E52.10.0.23", {"start": v(-48.5, 57.9) * mm, "end": v(-50.78, 57.9) * mm});
            skLineSegment(sketch, "E52.11.0.0", {"start": v(50.82, 53.1) * mm, "end": v(25.42, 53.33) * mm});
            skLineSegment(sketch, "E52.11.0.1", {"start": v(-21.57, 53.33) * mm, "end": v(21.61, 53.33) * mm});
            skArc(sketch, "E52.11.0.2", {"start": v(25.42, 53.33) * mm, "mid": v(24.14, 52.06) * mm, "end": v(25.42, 50.8) * mm});
            skArc(sketch, "E52.11.0.3", {"start": v(21.61, 53.33) * mm, "mid": v(22.88, 52.06) * mm, "end": v(21.61, 50.8) * mm});
            skLineSegment(sketch, "E52.11.0.4", {"start": v(50.82, 50.8) * mm, "end": v(25.42, 50.8) * mm});
            skLineSegment(sketch, "E52.11.0.5", {"start": v(48.53, 48.76) * mm, "end": v(50.82, 48.76) * mm});
            skArc(sketch, "E52.11.0.6", {"start": v(48.53, 48.76) * mm, "mid": v(47.26, 47.5) * mm, "end": v(48.53, 46.22) * mm});
            skArc(sketch, "E52.11.0.7", {"start": v(45.1, 48.76) * mm, "mid": v(46.38, 47.5) * mm, "end": v(45.1, 46.22) * mm});
            skLineSegment(sketch, "E52.11.0.8", {"start": v(48.53, 46.22) * mm, "end": v(50.82, 46.22) * mm});
            skLineSegment(sketch, "E52.11.0.9", {"start": v(45.1, 46.22) * mm, "end": v(1.93, 46.22) * mm});
            skLineSegment(sketch, "E52.11.0.10", {"start": v(45.1, 48.76) * mm, "end": v(1.93, 48.76) * mm});
            skLineSegment(sketch, "E52.11.0.11", {"start": v(-21.57, 50.8) * mm, "end": v(21.61, 50.8) * mm});
            skArc(sketch, "E52.11.0.12", {"start": v(1.93, 48.76) * mm, "mid": v(0.66, 47.5) * mm, "end": v(1.93, 46.22) * mm});
            skArc(sketch, "E52.11.0.13", {"start": v(-1.88, 48.76) * mm, "mid": v(-0.61, 47.5) * mm, "end": v(-1.88, 46.22) * mm});
            skLineSegment(sketch, "E52.11.0.14", {"start": v(-45.06, 48.76) * mm, "end": v(-1.88, 48.76) * mm});
            skLineSegment(sketch, "E52.11.0.15", {"start": v(-45.06, 46.22) * mm, "end": v(-1.88, 46.22) * mm});
            skLineSegment(sketch, "E52.11.0.16", {"start": v(-50.78, 53.33) * mm, "end": v(-25.38, 53.33) * mm});
            skArc(sketch, "E52.11.0.17", {"start": v(-25.38, 53.33) * mm, "mid": v(-24.1, 52.06) * mm, "end": v(-25.38, 50.8) * mm});
            skArc(sketch, "E52.11.0.18", {"start": v(-21.57, 53.33) * mm, "mid": v(-22.84, 52.06) * mm, "end": v(-21.57, 50.8) * mm});
            skLineSegment(sketch, "E52.11.0.19", {"start": v(-50.78, 50.8) * mm, "end": v(-25.38, 50.8) * mm});
            skArc(sketch, "E52.11.0.20", {"start": v(-45.06, 48.76) * mm, "mid": v(-46.33, 47.5) * mm, "end": v(-45.06, 46.22) * mm});
            skArc(sketch, "E52.11.0.21", {"start": v(-48.5, 48.76) * mm, "mid": v(-47.22, 47.5) * mm, "end": v(-48.5, 46.22) * mm});
            skLineSegment(sketch, "E52.11.0.22", {"start": v(-48.5, 46.22) * mm, "end": v(-50.78, 46.22) * mm});
            skLineSegment(sketch, "E52.11.0.23", {"start": v(-48.5, 48.76) * mm, "end": v(-50.78, 48.76) * mm});
            skLineSegment(sketch, "E52.12.0.0", {"start": v(50.82, 43.96) * mm, "end": v(25.42, 44.2) * mm});
            skLineSegment(sketch, "E52.12.0.1", {"start": v(-21.57, 44.19) * mm, "end": v(21.61, 44.19) * mm});
            skArc(sketch, "E52.12.0.2", {"start": v(25.42, 44.2) * mm, "mid": v(24.14, 42.92) * mm, "end": v(25.42, 41.65) * mm});
            skArc(sketch, "E52.12.0.3", {"start": v(21.61, 44.19) * mm, "mid": v(22.88, 42.92) * mm, "end": v(21.61, 41.65) * mm});
            skLineSegment(sketch, "E52.12.0.4", {"start": v(50.82, 41.65) * mm, "end": v(25.42, 41.65) * mm});
            skLineSegment(sketch, "E52.12.0.5", {"start": v(48.53, 39.62) * mm, "end": v(50.82, 39.62) * mm});
            skArc(sketch, "E52.12.0.6", {"start": v(48.53, 39.62) * mm, "mid": v(47.26, 38.35) * mm, "end": v(48.53, 37.08) * mm});
            skArc(sketch, "E52.12.0.7", {"start": v(45.1, 39.62) * mm, "mid": v(46.38, 38.35) * mm, "end": v(45.1, 37.08) * mm});
            skLineSegment(sketch, "E52.12.0.8", {"start": v(48.53, 37.08) * mm, "end": v(50.82, 37.08) * mm});
            skLineSegment(sketch, "E52.12.0.9", {"start": v(45.1, 37.08) * mm, "end": v(1.93, 37.08) * mm});
            skLineSegment(sketch, "E52.12.0.10", {"start": v(45.1, 39.62) * mm, "end": v(1.93, 39.62) * mm});
            skLineSegment(sketch, "E52.12.0.11", {"start": v(-21.57, 41.65) * mm, "end": v(21.61, 41.65) * mm});
            skArc(sketch, "E52.12.0.12", {"start": v(1.93, 39.62) * mm, "mid": v(0.66, 38.35) * mm, "end": v(1.93, 37.08) * mm});
            skArc(sketch, "E52.12.0.13", {"start": v(-1.88, 39.62) * mm, "mid": v(-0.61, 38.35) * mm, "end": v(-1.88, 37.08) * mm});
            skLineSegment(sketch, "E52.12.0.14", {"start": v(-45.06, 39.62) * mm, "end": v(-1.88, 39.62) * mm});
            skLineSegment(sketch, "E52.12.0.15", {"start": v(-45.06, 37.08) * mm, "end": v(-1.88, 37.08) * mm});
            skLineSegment(sketch, "E52.12.0.16", {"start": v(-50.78, 44.19) * mm, "end": v(-25.38, 44.19) * mm});
            skArc(sketch, "E52.12.0.17", {"start": v(-25.38, 44.19) * mm, "mid": v(-24.1, 42.92) * mm, "end": v(-25.38, 41.65) * mm});
            skArc(sketch, "E52.12.0.18", {"start": v(-21.57, 44.19) * mm, "mid": v(-22.84, 42.92) * mm, "end": v(-21.57, 41.65) * mm});
            skLineSegment(sketch, "E52.12.0.19", {"start": v(-50.78, 41.65) * mm, "end": v(-25.38, 41.65) * mm});
            skArc(sketch, "E52.12.0.20", {"start": v(-45.06, 39.62) * mm, "mid": v(-46.33, 38.35) * mm, "end": v(-45.06, 37.08) * mm});
            skArc(sketch, "E52.12.0.21", {"start": v(-48.5, 39.62) * mm, "mid": v(-47.22, 38.35) * mm, "end": v(-48.5, 37.08) * mm});
            skLineSegment(sketch, "E52.12.0.22", {"start": v(-48.5, 37.08) * mm, "end": v(-50.78, 37.08) * mm});
            skLineSegment(sketch, "E52.12.0.23", {"start": v(-48.5, 39.62) * mm, "end": v(-50.78, 39.62) * mm});
            skLineSegment(sketch, "E52.direction1", {"start": v(25.42, 153.92) * mm, "end": v(25.42, 144.77) * mm, "construction": true});
            skLineSegment(sketch, "E53.trimOffspring", {"start": v(-50.78, 153.92) * mm, "end": v(-50.78, 155.95) * mm});
            skLineSegment(sketch, "E54.trimOffspring", {"start": v(-50.78, 149.35) * mm, "end": v(-50.78, 151.38) * mm});
            skLineSegment(sketch, "E55.trimOffspring", {"start": v(-50.78, 144.77) * mm, "end": v(-50.78, 146.8) * mm});
            skLineSegment(sketch, "E56.trimOffspring", {"start": v(-50.78, 140.2) * mm, "end": v(-50.78, 142.23) * mm});
            skLineSegment(sketch, "E57.trimOffspring", {"start": v(-50.78, 135.63) * mm, "end": v(-50.78, 137.66) * mm});
            skLineSegment(sketch, "E58.trimOffspring", {"start": v(-50.78, 131.06) * mm, "end": v(-50.78, 133.09) * mm});
            skLineSegment(sketch, "E59.trimOffspring", {"start": v(-50.78, 126.49) * mm, "end": v(-50.78, 128.52) * mm});
            skLineSegment(sketch, "E60.trimOffspring", {"start": v(-50.78, 121.91) * mm, "end": v(-50.78, 123.95) * mm});
            skLineSegment(sketch, "E61.trimOffspring", {"start": v(-50.78, 117.34) * mm, "end": v(-50.78, 119.37) * mm});
            skLineSegment(sketch, "E62.trimOffspring", {"start": v(-50.78, 112.77) * mm, "end": v(-50.78, 114.8) * mm});
            skLineSegment(sketch, "E63.trimOffspring", {"start": v(-50.78, 108.2) * mm, "end": v(-50.78, 110.23) * mm});
            skLineSegment(sketch, "E64.trimOffspring", {"start": v(-50.78, 103.63) * mm, "end": v(-50.78, 105.66) * mm});
            skLineSegment(sketch, "E65.trimOffspring", {"start": v(-50.78, 99.05) * mm, "end": v(-50.78, 101.09) * mm});
            skLineSegment(sketch, "E66.trimOffspring", {"start": v(-50.78, 94.48) * mm, "end": v(-50.78, 96.51) * mm});
            skLineSegment(sketch, "E67.trimOffspring", {"start": v(-50.78, 89.9) * mm, "end": v(-50.78, 91.94) * mm});
            skLineSegment(sketch, "E68.trimOffspring", {"start": v(-50.78, 85.34) * mm, "end": v(-50.78, 87.37) * mm});
            skLineSegment(sketch, "E69.trimOffspring", {"start": v(-50.78, 67.05) * mm, "end": v(-50.78, 69.08) * mm});
            skLineSegment(sketch, "E70.trimOffspring", {"start": v(-50.78, 71.62) * mm, "end": v(-50.78, 73.65) * mm});
            skLineSegment(sketch, "E71.trimOffspring", {"start": v(-50.78, 76.2) * mm, "end": v(-50.78, 78.23) * mm});
            skLineSegment(sketch, "E72.trimOffspring", {"start": v(-50.78, 62.48) * mm, "end": v(-50.78, 64.5) * mm});
            skLineSegment(sketch, "E73.trimOffspring", {"start": v(-50.78, 57.9) * mm, "end": v(-50.78, 59.94) * mm});
            skLineSegment(sketch, "E74.trimOffspring", {"start": v(-50.78, 39.62) * mm, "end": v(-50.78, 41.65) * mm});
            skLineSegment(sketch, "E75.trimOffspring", {"start": v(-50.78, 53.33) * mm, "end": v(-50.78, 55.37) * mm});
            skLineSegment(sketch, "E76.trimOffspring", {"start": v(-50.78, 48.76) * mm, "end": v(-50.78, 50.8) * mm});
            skLineSegment(sketch, "E77.trimOffspring", {"start": v(-50.78, 44.19) * mm, "end": v(-50.78, 46.22) * mm});
            skLineSegment(sketch, "E78.trimOffspring", {"start": v(-50.78, 80.77) * mm, "end": v(-50.78, 82.8) * mm});
            skLineSegment(sketch, "E79.trimOffspring", {"start": v(50.82, 153.68) * mm, "end": v(50.82, 155.95) * mm});
            skLineSegment(sketch, "E80.trimOffspring", {"start": v(50.82, 149.35) * mm, "end": v(50.82, 151.38) * mm});
            skLineSegment(sketch, "E81.trimOffspring", {"start": v(50.82, 144.54) * mm, "end": v(50.82, 146.8) * mm});
            skLineSegment(sketch, "E82.trimOffspring", {"start": v(50.82, 140.2) * mm, "end": v(50.82, 142.23) * mm});
            skLineSegment(sketch, "E83.trimOffspring", {"start": v(50.82, 135.4) * mm, "end": v(50.82, 137.66) * mm});
            skLineSegment(sketch, "E84.trimOffspring", {"start": v(50.82, 131.06) * mm, "end": v(50.82, 133.09) * mm});
            skLineSegment(sketch, "E85.trimOffspring", {"start": v(50.82, 121.91) * mm, "end": v(50.82, 123.95) * mm});
            skLineSegment(sketch, "E86.trimOffspring", {"start": v(50.82, 126.25) * mm, "end": v(50.82, 128.52) * mm});
            skLineSegment(sketch, "E87.trimOffspring", {"start": v(50.82, 117.1) * mm, "end": v(50.82, 119.37) * mm});
            skLineSegment(sketch, "E88.trimOffspring", {"start": v(50.82, 112.77) * mm, "end": v(50.82, 114.8) * mm});
            skLineSegment(sketch, "E89.trimOffspring", {"start": v(50.82, 107.96) * mm, "end": v(50.82, 110.23) * mm});
            skLineSegment(sketch, "E90.trimOffspring", {"start": v(50.82, 103.63) * mm, "end": v(50.82, 105.66) * mm});
            skLineSegment(sketch, "E91.trimOffspring", {"start": v(50.82, 98.82) * mm, "end": v(50.82, 101.09) * mm});
            skLineSegment(sketch, "E92.trimOffspring", {"start": v(50.82, 94.48) * mm, "end": v(50.82, 96.51) * mm});
            skLineSegment(sketch, "E93.trimOffspring", {"start": v(50.82, 89.68) * mm, "end": v(50.82, 91.94) * mm});
            skLineSegment(sketch, "E94.trimOffspring", {"start": v(50.82, 85.34) * mm, "end": v(50.82, 87.37) * mm});
            skLineSegment(sketch, "E95.trimOffspring", {"start": v(50.82, 80.53) * mm, "end": v(50.82, 82.8) * mm});
            skLineSegment(sketch, "E96.trimOffspring", {"start": v(50.82, 76.2) * mm, "end": v(50.82, 78.23) * mm});
            skLineSegment(sketch, "E97.trimOffspring", {"start": v(50.82, 71.39) * mm, "end": v(50.82, 73.65) * mm});
            skLineSegment(sketch, "E98.trimOffspring", {"start": v(50.82, 67.05) * mm, "end": v(50.82, 69.08) * mm});
            skLineSegment(sketch, "E99.trimOffspring", {"start": v(50.82, 62.24) * mm, "end": v(50.82, 64.5) * mm});
            skLineSegment(sketch, "E100.trimOffspring", {"start": v(50.82, 57.9) * mm, "end": v(50.82, 59.94) * mm});
            skLineSegment(sketch, "E101.trimOffspring", {"start": v(50.82, 53.1) * mm, "end": v(50.82, 55.37) * mm});
            skLineSegment(sketch, "E102.trimOffspring", {"start": v(50.82, 48.76) * mm, "end": v(50.82, 50.8) * mm});
            skLineSegment(sketch, "E103.trimOffspring", {"start": v(50.82, 43.96) * mm, "end": v(50.82, 46.22) * mm});
            skLineSegment(sketch, "E104.trimOffspring", {"start": v(50.82, 39.62) * mm, "end": v(50.82, 41.65) * mm});
            skSolve(sketch);
        }
        {
            var Q0;
            Q0=makeQuery(id+"F0.imprint","IMPRINT",FACE,{"disambiguationData":[TD([[makeQuery(id+"F0.imprint","IMPRINT",EDGE,{"derivedFrom":sQuery(id+"F0.wireOp",EDGE,"E24.bottom")}),1.0]])]});
            var Q1;
            Q1=makeQuery(id+"F0.imprint","IMPRINT",FACE,{"disambiguationData":[TD([[makeQuery(id+"F0.imprint","IMPRINT",EDGE,{"derivedFrom":sQuery(id+"F0.wireOp",EDGE,"E0.top")}),-1.0]])]});
            var Q2;
            {var subQ50=sQuery(id+"F0.wireOp",EDGE,"E22.bottom");Q2=makeQuery(id+"F0.imprint","IMPRINT",FACE,{"disambiguationData":[TD([[makeQuery(id+"F0.imprint","IMPRINT",EDGE,{"derivedFrom":subQ50}),1.0]])]});}
            extrude(context, id + "F1", {"entities" : qUnion([Q0, Q1, Q2]), "depth" : 2.97 * mm});
        }
    });
